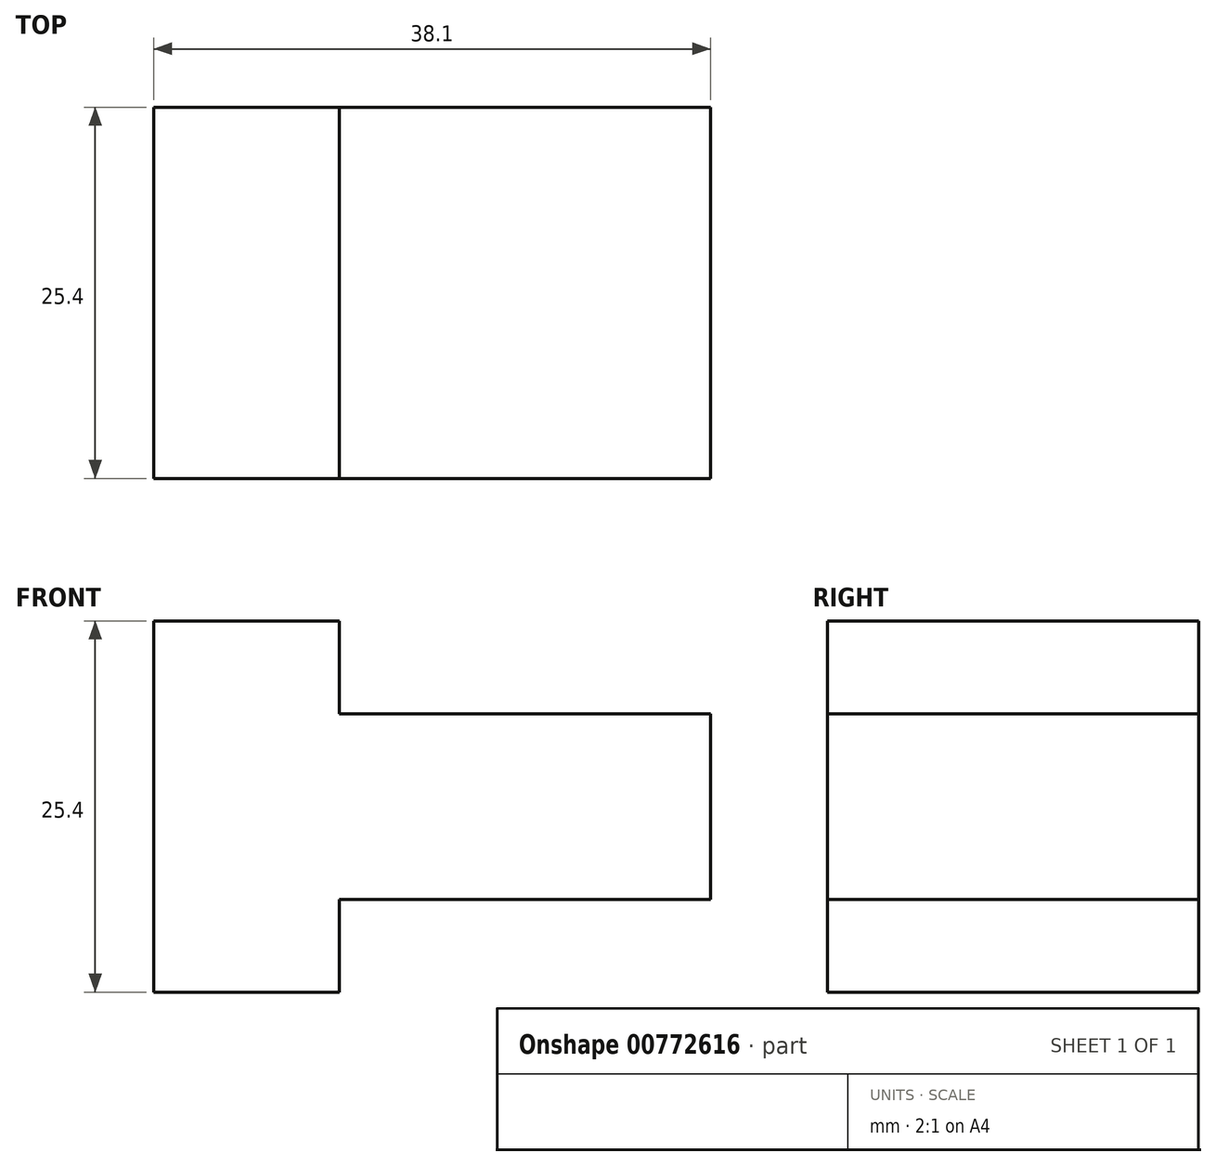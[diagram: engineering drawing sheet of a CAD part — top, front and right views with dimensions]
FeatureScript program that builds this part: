
annotation { "Feature Type Name" : "Feature", "Feature Type Description" : "" }
export const myFeature = defineFeature(function(context is Context, id is Id, definition is map)
    precondition{}
    {
        {
            var Q0;
            Q0=qCreatedBy(makeId("Front.planeOp"),FACE);
            var sketch = newSketch(context, id + "F0", { "sketchPlane" : qUnion([Q0])});
            skLineSegment(sketch, "E0", {"start": v(0, 0) * mm, "end": v(0, 25.4) * mm});
            skLineSegment(sketch, "E1", {"start": v(0, 25.4) * mm, "end": v(12.7, 25.4) * mm});
            skLineSegment(sketch, "E2", {"start": v(12.7, 25.4) * mm, "end": v(12.7, 19.05) * mm});
            skLineSegment(sketch, "E3", {"start": v(12.7, 19.05) * mm, "end": v(38.1, 19.05) * mm});
            skLineSegment(sketch, "E4", {"start": v(38.1, 19.05) * mm, "end": v(38.1, 6.35) * mm});
            skLineSegment(sketch, "E5", {"start": v(38.1, 6.35) * mm, "end": v(12.7, 6.35) * mm});
            skLineSegment(sketch, "E6", {"start": v(12.7, 6.35) * mm, "end": v(12.7, 0) * mm});
            skLineSegment(sketch, "E7", {"start": v(12.7, 0) * mm, "end": v(0, 0) * mm});
            skSolve(sketch);
        }
        {
            var Q0;
            Q0=makeQuery(id+"F0.imprint","IMPRINT",FACE,{"disambiguationData":[TD([[makeQuery(id+"F0.imprint","IMPRINT",EDGE,{"derivedFrom":sQuery(id+"F0.wireOp",EDGE,"E0")}),-1.0]])]});
            extrude(context, id + "F1", {"entities" : qUnion([Q0]), "depth" : 25.4 * mm, "offsetDistance" : 25.4 * mm});
        }
    });
